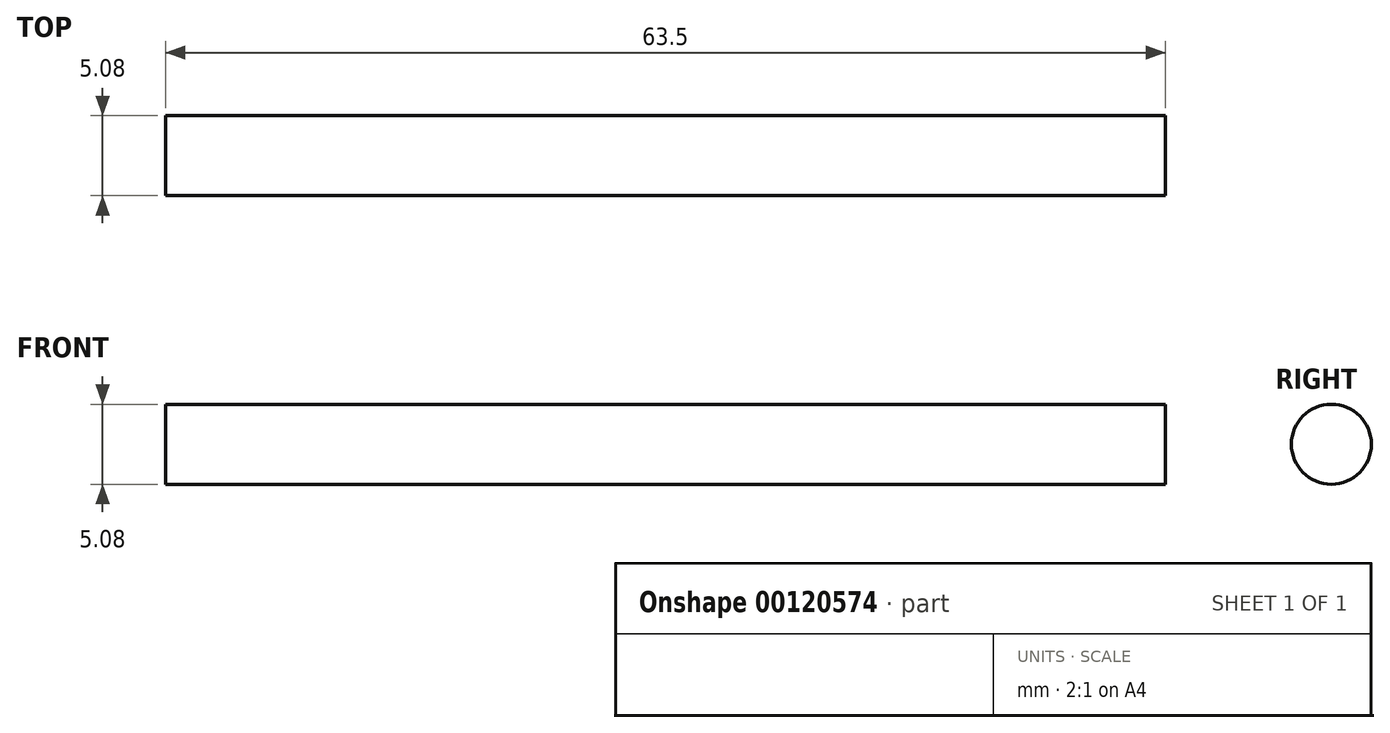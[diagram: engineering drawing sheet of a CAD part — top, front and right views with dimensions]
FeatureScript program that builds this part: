
annotation { "Feature Type Name" : "Feature", "Feature Type Description" : "" }
export const myFeature = defineFeature(function(context is Context, id is Id, definition is map)
    precondition{}
    {
        {
            var Q0;
            Q0=qCreatedBy(makeId("Front.planeOp"),FACE);
            var sketch = newSketch(context, id + "F0", { "sketchPlane" : qUnion([Q0])});
            skLineSegment(sketch, "E0", {"start": v(0, 0) * mm, "end": v(0, 2.54) * mm});
            skLineSegment(sketch, "E1", {"start": v(0, 2.54) * mm, "end": v(63.5, 2.54) * mm});
            skLineSegment(sketch, "E2", {"start": v(63.5, 2.54) * mm, "end": v(63.5, 0) * mm});
            skLineSegment(sketch, "E3", {"start": v(63.5, 0) * mm, "end": v(0, 0) * mm});
            skLineSegment(sketch, "E4", {"start": v(0, 0) * mm, "end": v(-37.1, 0) * mm, "construction": true});
            skSolve(sketch);
        }
        {
            var Q0;
            Q0 = qSketchRegion(id + "F0", true);
            var Q1;
            Q1=sQuery(id+"F0.wireOp",EDGE,"E4");
            revolve(context, id + "F1", {"entities" : qUnion([Q0]), "axis" : qUnion([Q1]), "revolveType" : RevolveType.FULL});
        }
    });
